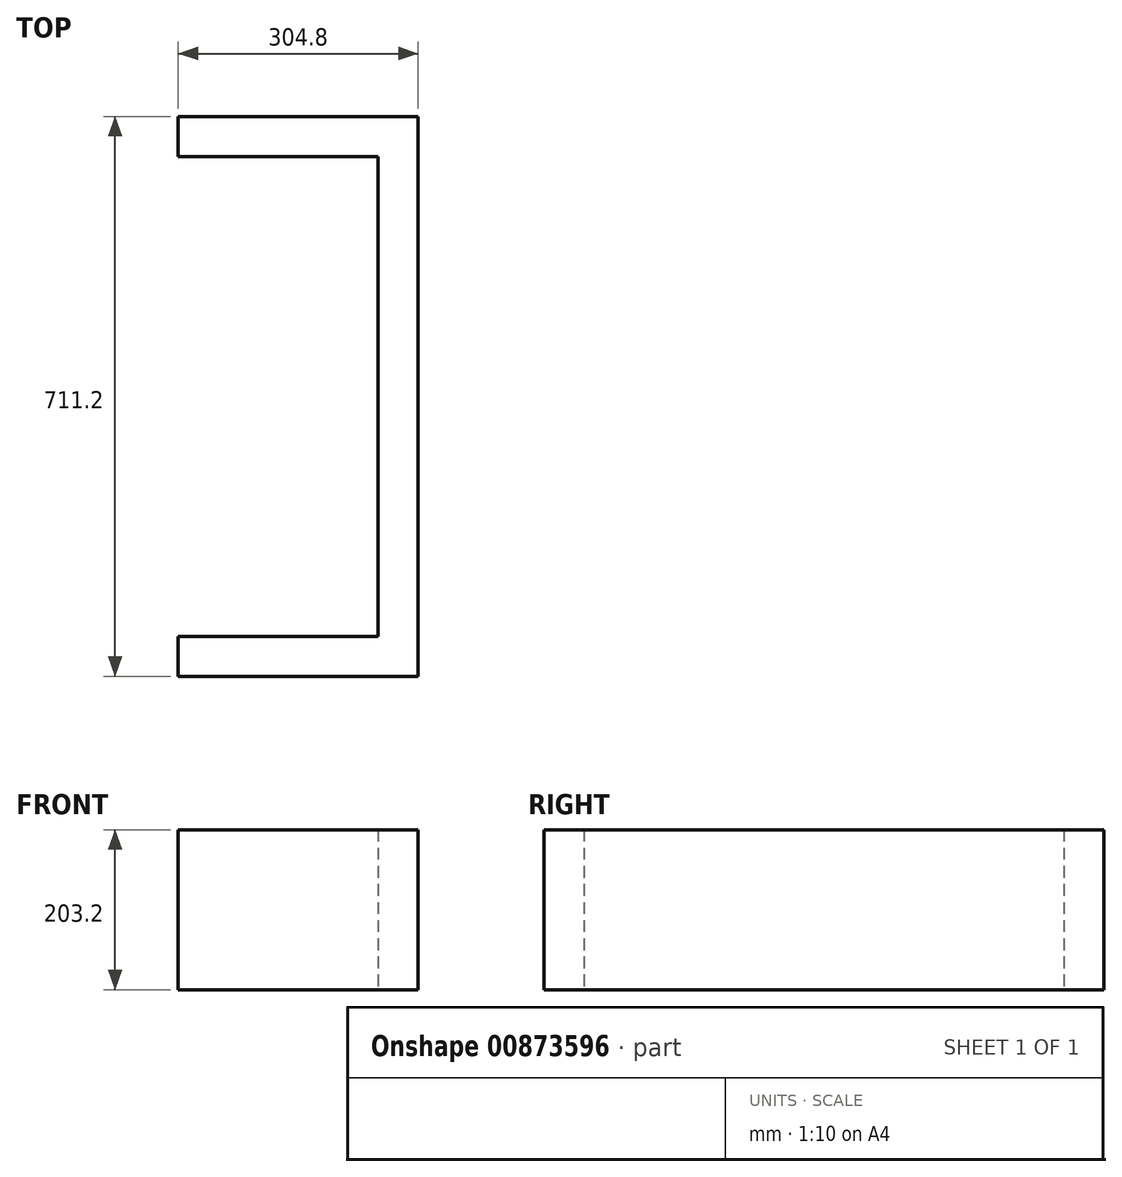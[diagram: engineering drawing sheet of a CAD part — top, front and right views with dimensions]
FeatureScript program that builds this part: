
annotation { "Feature Type Name" : "Feature", "Feature Type Description" : "" }
export const myFeature = defineFeature(function(context is Context, id is Id, definition is map)
    precondition{}
    {
        {
            var Q0;
            Q0=qCreatedBy(makeId("Top.planeOp"),FACE);
            var sketch = newSketch(context, id + "F0", { "sketchPlane" : qUnion([Q0])});
            skLineSegment(sketch, "E0.bottom", {"start": v(0, 0) * mm, "end": v(304.8, 0) * mm});
            skLineSegment(sketch, "E0.top", {"start": v(0, 50.8) * mm, "end": v(304.8, 50.8) * mm});
            skLineSegment(sketch, "E0.left", {"start": v(0, 0) * mm, "end": v(0, 50.8) * mm});
            skLineSegment(sketch, "E0.right", {"start": v(304.8, 0) * mm, "end": v(304.8, 50.8) * mm});
            skLineSegment(sketch, "E1.bottom", {"start": v(304.8, 0) * mm, "end": v(254, 0) * mm});
            skLineSegment(sketch, "E1.top", {"start": v(304.8, -609.6) * mm, "end": v(254, -609.6) * mm});
            skLineSegment(sketch, "E1.left", {"start": v(304.8, 0) * mm, "end": v(304.8, -609.6) * mm});
            skLineSegment(sketch, "E1.right", {"start": v(254, 0) * mm, "end": v(254, -609.6) * mm});
            skLineSegment(sketch, "E2.bottom", {"start": v(304.8, -609.6) * mm, "end": v(0, -609.6) * mm});
            skLineSegment(sketch, "E2.top", {"start": v(304.8, -660.4) * mm, "end": v(0, -660.4) * mm});
            skLineSegment(sketch, "E2.left", {"start": v(304.8, -609.6) * mm, "end": v(304.8, -660.4) * mm});
            skLineSegment(sketch, "E2.right", {"start": v(0, -609.6) * mm, "end": v(0, -660.4) * mm});
            skSolve(sketch);
        }
        {
            var Q0;
            Q0 = qSketchRegion(id + "F0", true);
            extrude(context, id + "F1", {"entities" : qUnion([Q0]), "depth" : 203.2 * mm, "offsetDistance" : 25.4 * mm});
        }
    });
